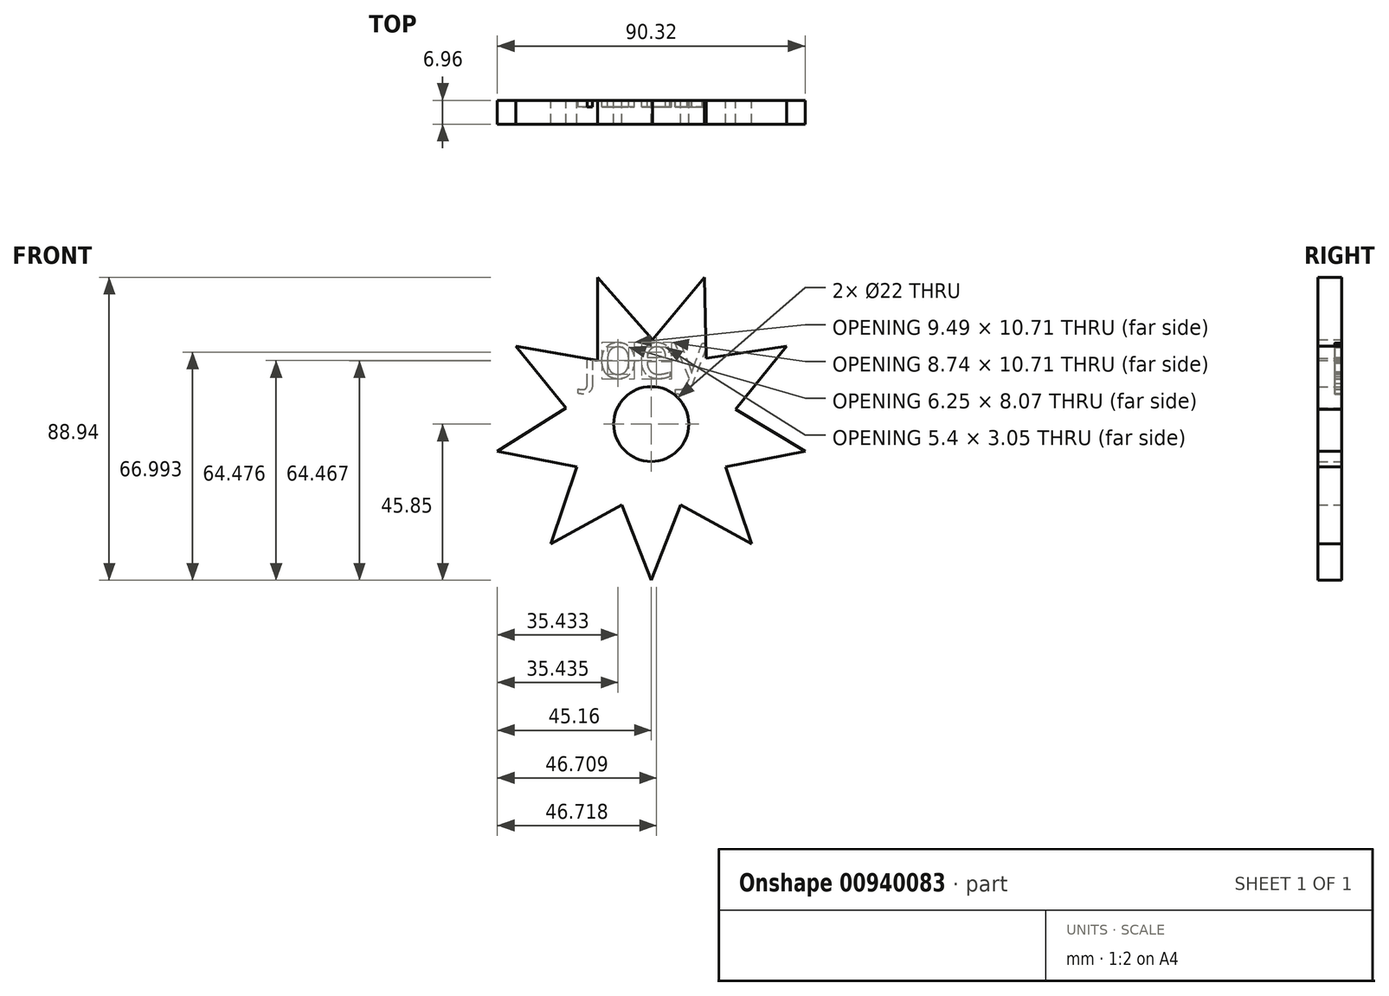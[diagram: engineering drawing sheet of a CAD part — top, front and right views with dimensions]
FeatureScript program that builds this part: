
annotation { "Feature Type Name" : "Feature", "Feature Type Description" : "" }
export const myFeature = defineFeature(function(context is Context, id is Id, definition is map)
    precondition{}
    {
        {
            var Q0;
            Q0=qCreatedBy(makeId("Front.planeOp"),FACE);
            var sketch = newSketch(context, id + "F0", { "sketchPlane" : qUnion([Q0])});
            skArc(sketch, "E0", {"start": v(-10.12, 36.73) * mm, "mid": v(-12.95, 35.83) * mm, "end": v(-15.7, 34.72) * mm});
            skArc(sketch, "E1", {"start": v(-4.96, 30.85) * mm, "mid": v(-10.5, 29.43) * mm, "end": v(-15.7, 27.02) * mm});
            skCircle(sketch, "E2", {"center": v(0, 0) * mm, "radius": 11 * mm});
            skArc(sketch, "E3.cCircle", {"start": v(-13.73, 40.84) * mm, "mid": v(-14.72, 40.5) * mm, "end": v(-15.7, 40.13) * mm, "construction": true});
            skPoint(sketch, "E3.0.midPoint", {"position": v(37.32, -21.54) * mm});
            skLineSegment(sketch, "E4", {"start": v(15.67, 43.1) * mm, "end": v(10.68, 29.36) * mm});
            skLineSegment(sketch, "E5", {"start": v(-15.7, 43.09) * mm, "end": v(-15.7, 10.62) * mm});
            skLineSegment(sketch, "E6", {"start": v(-15.7, 10.62) * mm, "end": v(-15.7, 43.09) * mm});
            skLineSegment(sketch, "E7", {"start": v(-15.7, 43.09) * mm, "end": v(0.78, 24.3) * mm});
            skLineSegment(sketch, "E8", {"start": v(15.02, 19.13) * mm, "end": v(39.7, 22.94) * mm});
            skLineSegment(sketch, "E9", {"start": v(18.66, -3.29) * mm, "end": v(39.7, 22.94) * mm});
            skLineSegment(sketch, "E10", {"start": v(29.48, -35.12) * mm, "end": v(18.66, -3.29) * mm});
            skLineSegment(sketch, "E11", {"start": v(29.48, -35.12) * mm, "end": v(0, -18.95) * mm});
            skLineSegment(sketch, "E12", {"start": v(0, -18.95) * mm, "end": v(-29.47, -35.13) * mm});
            skLineSegment(sketch, "E13", {"start": v(-18.66, -3.3) * mm, "end": v(-29.47, -35.13) * mm});
            skLineSegment(sketch, "E14", {"start": v(-39.72, 22.92) * mm, "end": v(-18.66, -3.3) * mm});
            skLineSegment(sketch, "E15", {"start": v(-39.72, 22.92) * mm, "end": v(-6.2, 17.02) * mm});
            skLineSegment(sketch, "E16", {"start": v(-6.2, 17.02) * mm, "end": v(15.67, 43.1) * mm});
            skLineSegment(sketch, "E17", {"start": v(16.22, 18.12) * mm, "end": v(15.67, 43.1) * mm});
            skLineSegment(sketch, "E18", {"start": v(16.4, 9.48) * mm, "end": v(45.16, -7.95) * mm});
            skLineSegment(sketch, "E19", {"start": v(12.18, -14.51) * mm, "end": v(45.16, -7.95) * mm});
            skLineSegment(sketch, "E20", {"start": v(12.18, -14.51) * mm, "end": v(0.01, -45.85) * mm});
            skLineSegment(sketch, "E21", {"start": v(-12.18, -14.51) * mm, "end": v(0.01, -45.85) * mm});
            skLineSegment(sketch, "E22", {"start": v(-12.18, -14.51) * mm, "end": v(-45.16, -7.97) * mm});
            skLineSegment(sketch, "E23", {"start": v(-15.7, 10.62) * mm, "end": v(-45.16, -7.97) * mm});
            skArc(sketch, "E24.trimOffspring", {"start": v(14.73, 40.5) * mm, "mid": v(14.25, 40.66) * mm, "end": v(13.77, 40.83) * mm, "construction": true});
            skArc(sketch, "E25.trimOffspring", {"start": v(15.86, 34.64) * mm, "mid": v(13.12, 35.77) * mm, "end": v(10.3, 36.68) * mm});
            skArc(sketch, "E26.trimOffspring", {"start": v(10.68, 29.36) * mm, "mid": v(8.05, 30.2) * mm, "end": v(5.35, 30.78) * mm});
            skArc(sketch, "E27.trimOffspring", {"start": v(34.42, 16.35) * mm, "mid": v(33.73, 17.72) * mm, "end": v(33, 19.06) * mm});
            skArc(sketch, "E28.trimOffspring", {"start": v(37.84, 20.61) * mm, "mid": v(37.58, 21.08) * mm, "end": v(37.31, 21.55) * mm, "construction": true});
            skArc(sketch, "E29.trimOffspring", {"start": v(29.52, 10.24) * mm, "mid": v(28.41, 13) * mm, "end": v(27.06, 15.63) * mm});
            skArc(sketch, "E30.trimOffspring", {"start": v(29.2, -11.13) * mm, "mid": v(30.77, -5.42) * mm, "end": v(31.24, 0.49) * mm});
            skArc(sketch, "E31.trimOffspring", {"start": v(36.87, -9.6) * mm, "mid": v(37.52, -6.6) * mm, "end": v(37.93, -3.57) * mm});
            skArc(sketch, "E32.trimOffspring", {"start": v(42.44, -7.47) * mm, "mid": v(42.53, -6.94) * mm, "end": v(42.61, -6.4) * mm, "construction": true});
            skArc(sketch, "E33.trimOffspring", {"start": v(15.21, -27.3) * mm, "mid": v(20.09, -23.93) * mm, "end": v(24.24, -19.7) * mm});
            skArc(sketch, "E34.trimOffspring", {"start": v(22.07, -31.05) * mm, "mid": v(24.5, -29.18) * mm, "end": v(26.76, -27.12) * mm});
            skArc(sketch, "E35.trimOffspring", {"start": v(26.87, -33.69) * mm, "mid": v(27.7, -33) * mm, "end": v(28.52, -32.3) * mm, "construction": true});
            skArc(sketch, "E36.trimOffspring", {"start": v(-1.07, -43.08) * mm, "mid": v(0.01, -43.09) * mm, "end": v(1.1, -43.08) * mm, "construction": true});
            skArc(sketch, "E37.trimOffspring", {"start": v(-3.05, -37.98) * mm, "mid": v(-1.52, -38.07) * mm, "end": v(0, -38.1) * mm});
            skArc(sketch, "E38.trimOffspring", {"start": v(-5.9, -30.69) * mm, "mid": v(0, -31.25) * mm, "end": v(5.9, -30.68) * mm});
            skArc(sketch, "E39.trimOffspring", {"start": v(-28.5, -32.31) * mm, "mid": v(-28.1, -32.67) * mm, "end": v(-27.69, -33.02) * mm, "construction": true});
            skArc(sketch, "E40.trimOffspring", {"start": v(-26.75, -27.13) * mm, "mid": v(-24.48, -29.2) * mm, "end": v(-22.06, -31.07) * mm});
            skArc(sketch, "E41.trimOffspring", {"start": v(-24.24, -19.72) * mm, "mid": v(-20.08, -23.94) * mm, "end": v(-15.2, -27.3) * mm});
            skArc(sketch, "E42.trimOffspring", {"start": v(-42.43, -7.5) * mm, "mid": v(-42.34, -8.02) * mm, "end": v(-42.23, -8.55) * mm, "construction": true});
            skArc(sketch, "E43.trimOffspring", {"start": v(-37.95, -3.42) * mm, "mid": v(-37.53, -6.54) * mm, "end": v(-36.87, -9.62) * mm});
            skArc(sketch, "E44.trimOffspring", {"start": v(-31.23, 0.81) * mm, "mid": v(-30.8, -5.26) * mm, "end": v(-29.2, -11.14) * mm});
            skArc(sketch, "E45.trimOffspring", {"start": v(-36.8, 22.4) * mm, "mid": v(-37.07, 21.97) * mm, "end": v(-37.32, 21.54) * mm, "construction": true});
            skArc(sketch, "E46.trimOffspring", {"start": v(-31.48, 21.47) * mm, "mid": v(-32.26, 20.27) * mm, "end": v(-33, 19.04) * mm});
            skArc(sketch, "E47.trimOffspring", {"start": v(-23.9, 20.13) * mm, "mid": v(-27.16, 15.44) * mm, "end": v(-29.52, 10.23) * mm});
            skLineSegment(sketch, "E48.trimOffspring", {"start": v(4.37, 12) * mm, "end": v(0, 0) * mm});
            skSolve(sketch);
        }
        {
            var Q0;
            Q0 = qSketchRegion(id + "F0", true);
            var Q1;
            Q1=makeQuery(id+"F0.imprint","IMPRINT",FACE,{"disambiguationData":[TD([[makeQuery(id+"F0.imprint","IMPRINT",EDGE,{"derivedFrom":sQuery(id+"F0.wireOp",EDGE,"vjdqNn5C-TanX-u8TL-A7RQ-eGto8MNXOIGU")}),1.0]])]});
            var Q2;
            Q2=makeQuery(id+"F0.imprint","IMPRINT",FACE,{"disambiguationData":[TD([[makeQuery(id+"F0.imprint","IMPRINT",EDGE,{"derivedFrom":sQuery(id+"F0.wireOp",EDGE,"E1")}),1.0]])]});
            var Q3;
            Q3=makeQuery(id+"F0.imprint","IMPRINT",FACE,{"disambiguationData":[TD([[makeQuery(id+"F0.imprint","IMPRINT",EDGE,{"derivedFrom":sQuery(id+"F0.wireOp",EDGE,"7N1TooFt-qj7Z-gajg-DGFD-n3986Qv0yqS9")}),1.0]])]});
            var Q4;
            Q4=makeQuery(id+"F0.imprint","IMPRINT",FACE,{"disambiguationData":[TD([[makeQuery(id+"F0.imprint","IMPRINT",EDGE,{"derivedFrom":sQuery(id+"F0.wireOp",EDGE,"QVbPmB0X-lL9W-tEFt-AnIZ-0DQRTlCJ8q27")}),1.0]])]});
            var Q5;
            {var subQ0=sQuery(id+"F0.wireOp",EDGE,"E6");var subQ1=sQuery(id+"F0.wireOp",EDGE,"vjdqNn5C-TanX-u8TL-A7RQ-eGto8MNXOIGU");var subQ2=makeQuery(id+"F0.imprint","INTERSECT",VERTEX,{"derivedFrom":[subQ1,subQ0]});Q5=makeQuery(id+"F0.imprint","IMPRINT",FACE,{"disambiguationData":[TD([[makeQuery(id+"F0.imprint","IMPRINT",EDGE,{"disambiguationData":[TD([[subQ2,-1.0]])],"derivedFrom":subQ1}),1.0]])]});}
            var Q6;
            {var subQ0=sQuery(id+"F0.wireOp",EDGE,"E8m2L5N2-aVOK-1Rgx-IlOn-zcTuEdM3rgLj");var subQ1=sQuery(id+"F0.wireOp",EDGE,"vjdqNn5C-TanX-u8TL-A7RQ-eGto8MNXOIGU");var subQ2=makeQuery(id+"F0.imprint","INTERSECT",VERTEX,{"derivedFrom":[subQ1,subQ0]});Q6=makeQuery(id+"F0.imprint","IMPRINT",FACE,{"disambiguationData":[TD([[makeQuery(id+"F0.imprint","IMPRINT",EDGE,{"disambiguationData":[TD([[subQ2,-1.0]])],"derivedFrom":subQ1}),1.0]])]});}
            var Q7;
            {var subQ1=sQuery(id+"F0.wireOp",EDGE,"E8m2L5N2-aVOK-1Rgx-IlOn-zcTuEdM3rgLj");var subQ3=sQuery(id+"F0.wireOp",EDGE,"QVbPmB0X-lL9W-tEFt-AnIZ-0DQRTlCJ8q27");var subQ4=makeQuery(id+"F0.imprint","INTERSECT",VERTEX,{"derivedFrom":[subQ3,subQ1]});Q7=makeQuery(id+"F0.imprint","IMPRINT",FACE,{"disambiguationData":[TD([[makeQuery(id+"F0.imprint","IMPRINT",EDGE,{"disambiguationData":[TD([[subQ4,-1.0]])],"derivedFrom":subQ3}),-1.0]])]});}
            var Q8;
            {var subQ3=sQuery(id+"F0.wireOp",EDGE,"amyiMip4-dRdH-KSsX-wdEF-xCskwHmIxN3R");var subQ5=sQuery(id+"F0.wireOp",EDGE,"QVbPmB0X-lL9W-tEFt-AnIZ-0DQRTlCJ8q27");var subQ6=makeQuery(id+"F0.imprint","INTERSECT",VERTEX,{"derivedFrom":[subQ5,subQ3]});Q8=makeQuery(id+"F0.imprint","IMPRINT",FACE,{"disambiguationData":[TD([[makeQuery(id+"F0.imprint","IMPRINT",EDGE,{"disambiguationData":[TD([[subQ6,-1.0]])],"derivedFrom":subQ5}),-1.0]])]});}
            var Q9;
            {var subQ0=sQuery(id+"F0.wireOp",EDGE,"E4");var subQ3=sQuery(id+"F0.wireOp",EDGE,"QVbPmB0X-lL9W-tEFt-AnIZ-0DQRTlCJ8q27");var subQ4=makeQuery(id+"F0.imprint","INTERSECT",VERTEX,{"derivedFrom":[subQ3,subQ0]});Q9=makeQuery(id+"F0.imprint","IMPRINT",FACE,{"disambiguationData":[TD([[makeQuery(id+"F0.imprint","IMPRINT",EDGE,{"disambiguationData":[TD([[subQ4,-1.0]])],"derivedFrom":subQ3}),-1.0]])]});}
            var Q10;
            {var subQ0=sQuery(id+"F0.wireOp",EDGE,"E4");var subQ5=sQuery(id+"F0.wireOp",EDGE,"QVbPmB0X-lL9W-tEFt-AnIZ-0DQRTlCJ8q27");var subQ6=makeQuery(id+"F0.imprint","INTERSECT",VERTEX,{"derivedFrom":[subQ5,subQ0]});Q10=makeQuery(id+"F0.imprint","IMPRINT",FACE,{"disambiguationData":[TD([[makeQuery(id+"F0.imprint","IMPRINT",EDGE,{"disambiguationData":[TD([[subQ6,1.0]])],"derivedFrom":subQ5}),-1.0]])]});}
            var Q11;
            {var subQ3=sQuery(id+"F0.wireOp",EDGE,"GVonU4fr-R4dB-ey45-qq7Z-7UyC5zTwUtaV");var subQ5=sQuery(id+"F0.wireOp",EDGE,"QVbPmB0X-lL9W-tEFt-AnIZ-0DQRTlCJ8q27");var subQ7=makeQuery(id+"F0.imprint","INTERSECT",VERTEX,{"derivedFrom":[subQ5,subQ3]});Q11=makeQuery(id+"F0.imprint","IMPRINT",FACE,{"disambiguationData":[TD([[makeQuery(id+"F0.imprint","IMPRINT",EDGE,{"disambiguationData":[TD([[subQ7,1.0]])],"derivedFrom":subQ5}),-1.0]])]});}
            var Q12;
            {var subQ3=sQuery(id+"F0.wireOp",EDGE,"rz5sVW3t-XlYD-3KQK-9teA-zIVZfDhuHufb");var subQ5=sQuery(id+"F0.wireOp",EDGE,"QVbPmB0X-lL9W-tEFt-AnIZ-0DQRTlCJ8q27");var subQ6=makeQuery(id+"F0.imprint","INTERSECT",VERTEX,{"derivedFrom":[subQ5,subQ3]});Q12=makeQuery(id+"F0.imprint","IMPRINT",FACE,{"disambiguationData":[TD([[makeQuery(id+"F0.imprint","IMPRINT",EDGE,{"disambiguationData":[TD([[subQ6,-1.0]])],"derivedFrom":subQ5}),-1.0]])]});}
            var Q13;
            {var subQ3=sQuery(id+"F0.wireOp",EDGE,"ABKx3fF0-R5xO-OdJY-aV8r-WT2jVfiVLmj3");var subQ5=sQuery(id+"F0.wireOp",EDGE,"QVbPmB0X-lL9W-tEFt-AnIZ-0DQRTlCJ8q27");var subQ6=makeQuery(id+"F0.imprint","INTERSECT",VERTEX,{"derivedFrom":[subQ5,subQ3]});Q13=makeQuery(id+"F0.imprint","IMPRINT",FACE,{"disambiguationData":[TD([[makeQuery(id+"F0.imprint","IMPRINT",EDGE,{"disambiguationData":[TD([[subQ6,-1.0]])],"derivedFrom":subQ5}),-1.0]])]});}
            var Q14;
            {var subQ3=sQuery(id+"F0.wireOp",EDGE,"E11");var subQ5=sQuery(id+"F0.wireOp",EDGE,"vjdqNn5C-TanX-u8TL-A7RQ-eGto8MNXOIGU");var subQ6=makeQuery(id+"F0.imprint","INTERSECT",VERTEX,{"derivedFrom":[subQ5,subQ3]});Q14=makeQuery(id+"F0.imprint","IMPRINT",FACE,{"disambiguationData":[TD([[makeQuery(id+"F0.imprint","IMPRINT",EDGE,{"disambiguationData":[TD([[subQ6,-1.0]])],"derivedFrom":subQ5}),1.0]])]});}
            var Q15;
            {var subQ0=sQuery(id+"F0.wireOp",EDGE,"E18");var subQ1=sQuery(id+"F0.wireOp",EDGE,"vjdqNn5C-TanX-u8TL-A7RQ-eGto8MNXOIGU");var subQ2=makeQuery(id+"F0.imprint","INTERSECT",VERTEX,{"derivedFrom":[subQ1,subQ0]});Q15=makeQuery(id+"F0.imprint","IMPRINT",FACE,{"disambiguationData":[TD([[makeQuery(id+"F0.imprint","IMPRINT",EDGE,{"disambiguationData":[TD([[subQ2,1.0]])],"derivedFrom":subQ1}),1.0]])]});}
            extrude(context, id + "F1", {"entities" : qUnion([Q0, Q1, Q2, Q3, Q4, Q5, Q6, Q7, Q8, Q9, Q10, Q11, Q12, Q13, Q14, Q15]), "depth" : 6.96 * mm, "offsetDistance" : 25 * mm});
        }
        {
            var Q0;
            Q0=qCreatedBy(makeId("Front.planeOp"),FACE);
            var sketch = newSketch(context, id + "F2", { "sketchPlane" : qUnion([Q0])});
            skText(sketch, "E49", { "text": "joey", "fontName": "OpenSans-Regular.ttf"});
            const initialGuessF2  = {"E49": [-0.02044, 0.01346, 1, 0, 0.0139]};
            skSetInitialGuess(sketch, initialGuessF2);
            skSolve(sketch);
        }
        {
            var Q0;
            Q0 = qSketchRegion(id + "F2", true);
            extrude(context, id + "F3", {"entities" : qUnion([Q0]), "operationType" : NewBodyOperationType.REMOVE, "depth" : 2 * mm, "offsetDistance" : 25 * mm});
        }
    });
